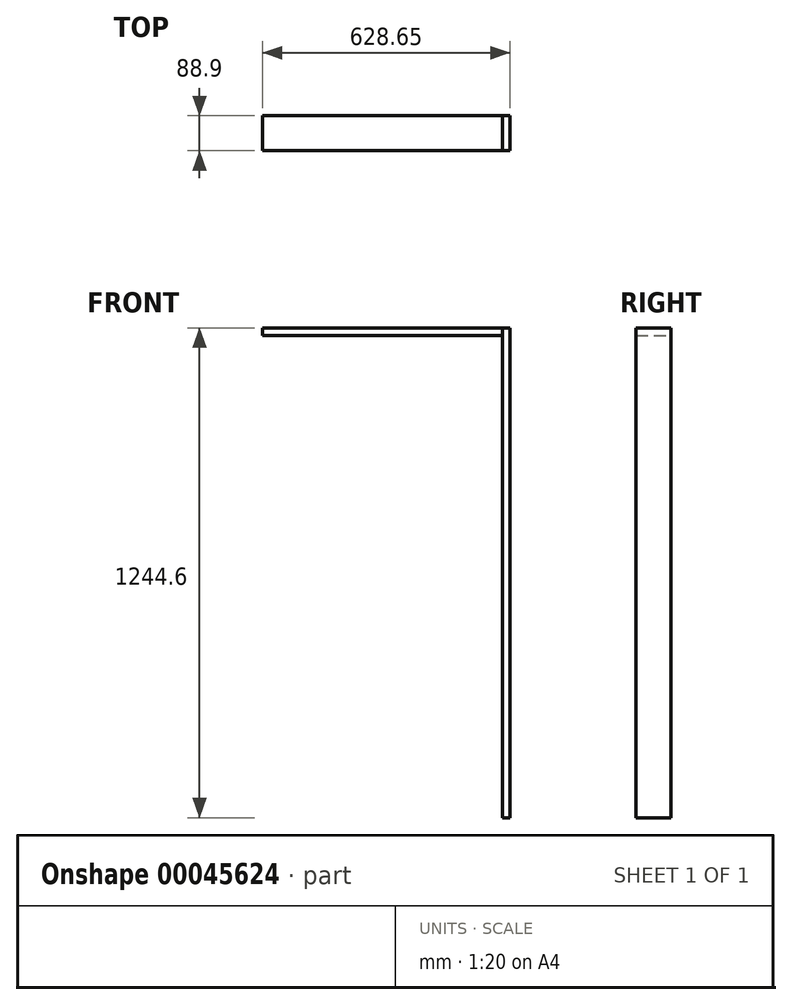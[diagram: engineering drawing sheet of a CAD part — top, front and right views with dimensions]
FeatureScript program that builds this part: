
annotation { "Feature Type Name" : "Feature", "Feature Type Description" : "" }
export const myFeature = defineFeature(function(context is Context, id is Id, definition is map)
    precondition{}
    {
        {
            var Q0;
            Q0=qCreatedBy(makeId("Front.planeOp"),FACE);
            var sketch = newSketch(context, id + "F0", { "sketchPlane" : qUnion([Q0])});
            skLineSegment(sketch, "E0", {"start": v(0, 19.05) * mm, "end": v(609.6, 19.05) * mm});
            skLineSegment(sketch, "E1", {"start": v(609.6, 19.05) * mm, "end": v(609.6, 0) * mm});
            skLineSegment(sketch, "E2", {"start": v(609.6, 0) * mm, "end": v(0, 0) * mm});
            skLineSegment(sketch, "E3", {"start": v(0, 0) * mm, "end": v(0, 19.05) * mm});
            skSolve(sketch);
        }
        {
            var Q0;
            Q0 = qSketchRegion(id + "F0", true);
            extrude(context, id + "F1", {"entities" : qUnion([Q0]), "depth" : 88.9 * mm});
        }
        {
            var Q0;
            Q0=makeQuery(id+"F1.opExtrude","CAP_FACE",FACE,{"disambiguationData":[OSD([sQuery(id+"F0.wireOp",EDGE,"E0"),sQuery(id+"F0.wireOp",EDGE,"E1"),sQuery(id+"F0.wireOp",EDGE,"E2"),sQuery(id+"F0.wireOp",EDGE,"E3")])],"isStart":true});
            var sketch = newSketch(context, id + "F2", { "sketchPlane" : qUnion([Q0])});
            skLineSegment(sketch, "E4", {"start": v(-609.6, 19.05) * mm, "end": v(-609.6, -1225.55) * mm});
            skLineSegment(sketch, "E5", {"start": v(-609.6, -1225.55) * mm, "end": v(-628.65, -1225.55) * mm});
            skLineSegment(sketch, "E6", {"start": v(-628.65, -1225.55) * mm, "end": v(-628.65, 19.05) * mm});
            skLineSegment(sketch, "E7", {"start": v(-628.65, 19.05) * mm, "end": v(-609.6, 19.05) * mm});
            skSolve(sketch);
        }
        {
            var Q0;
            {var subQ2=sQuery(id+"F2.wireOp",EDGE,"E5");Q0=makeQuery(id+"F2.imprint","IMPRINT",FACE,{"disambiguationData":[TD([[makeQuery(id+"F2.imprint","IMPRINT",EDGE,{"derivedFrom":subQ2}),-1.0]])]});}
            extrude(context, id + "F3", {"entities" : qUnion([Q0]), "oppositeDirection" : true, "depth" : 88.9 * mm});
        }
    });
